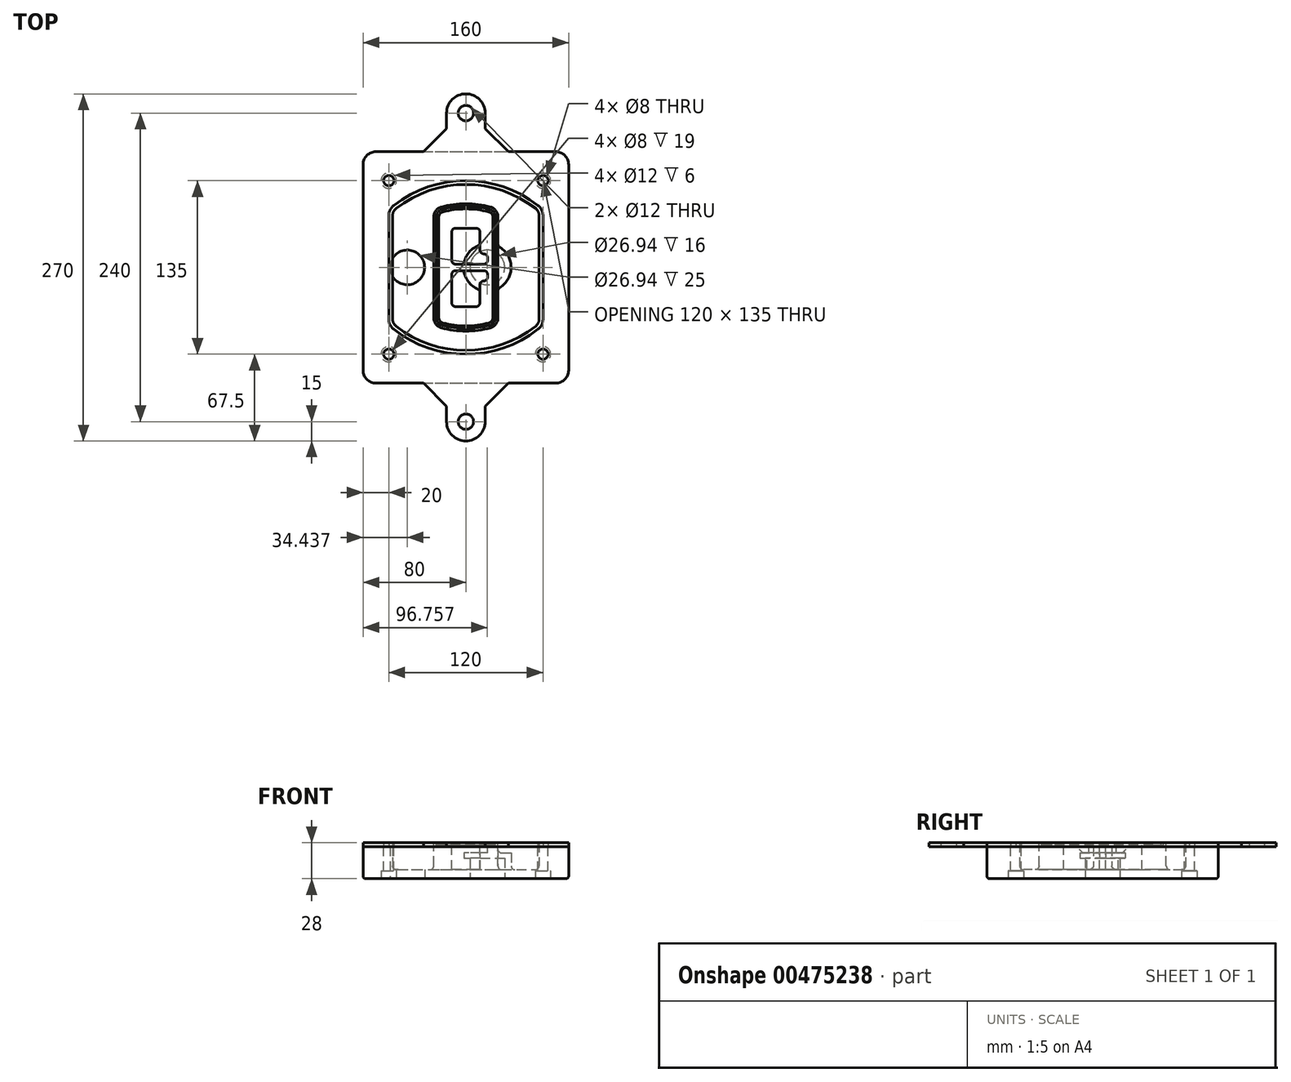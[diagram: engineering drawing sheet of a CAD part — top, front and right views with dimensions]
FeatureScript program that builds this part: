
annotation { "Feature Type Name" : "Feature", "Feature Type Description" : "" }
export const myFeature = defineFeature(function(context is Context, id is Id, definition is map)
    precondition{}
    {
        {
            var Q0;
            Q0=qCreatedBy(makeId("Top.planeOp"),FACE);
            var sketch = newSketch(context, id + "F0", { "sketchPlane" : qUnion([Q0])});
            skPoint(sketch, "E0.rect.middle", {"position": v(0, 0) * mm});
            skLineSegment(sketch, "E1.bottom", {"start": v(-70, -90) * mm, "end": v(70, -90) * mm});
            skLineSegment(sketch, "E1.top", {"start": v(-70, 90) * mm, "end": v(70, 90) * mm});
            skLineSegment(sketch, "E1.left", {"start": v(-80, -80) * mm, "end": v(-80, 80) * mm});
            skLineSegment(sketch, "E1.right", {"start": v(80, -80) * mm, "end": v(80, 80) * mm});
            skLineSegment(sketch, "E2", {"start": v(-80, 90) * mm, "end": v(80, -90) * mm, "construction": true});
            skLineSegment(sketch, "E3", {"start": v(80, 90) * mm, "end": v(-80, -90) * mm, "construction": true});
            skCircle(sketch, "E4", {"center": v(-60, 67.5) * mm, "radius": 4 * mm});
            skCircle(sketch, "E5", {"center": v(60, 67.5) * mm, "radius": 4 * mm});
            skCircle(sketch, "E6", {"center": v(60, -67.5) * mm, "radius": 4 * mm});
            skCircle(sketch, "E7", {"center": v(-60, -67.5) * mm, "radius": 4 * mm});
            skLineSegment(sketch, "E8", {"start": v(-60, 67.5) * mm, "end": v(60, 67.5) * mm, "construction": true});
            skLineSegment(sketch, "E9", {"start": v(60, 67.5) * mm, "end": v(60, -67.5) * mm, "construction": true});
            skLineSegment(sketch, "E10", {"start": v(60, -67.5) * mm, "end": v(-60, -67.5) * mm, "construction": true});
            skLineSegment(sketch, "E11", {"start": v(-60, -67.5) * mm, "end": v(-60, 67.5) * mm, "construction": true});
            skLineSegment(sketch, "E12", {"start": v(-60, 40.3) * mm, "end": v(-60, -40.3) * mm});
            skLineSegment(sketch, "E13", {"start": v(60, 40.3) * mm, "end": v(60, -40.3) * mm});
            skArc(sketch, "E14", {"start": v(56.15, 48.18) * mm, "mid": v(0, 67.5) * mm, "end": v(-56.15, 48.18) * mm});
            skArc(sketch, "E15", {"start": v(-56.15, -48.18) * mm, "mid": v(0, -67.5) * mm, "end": v(56.15, -48.18) * mm});
            skLineSegment(sketch, "E16", {"start": v(-60, 0) * mm, "end": v(60, 0) * mm, "construction": true});
            skPoint(sketch, "E17.visualSharp", {"position": v(-60, -45) * mm});
            skArc(sketch, "E17.filletArc", {"start": v(-60, -40.3) * mm, "mid": v(-58.99, -44.68) * mm, "end": v(-56.15, -48.18) * mm});
            skPoint(sketch, "E18.visualSharp", {"position": v(-60, 45) * mm});
            skArc(sketch, "E18.filletArc", {"start": v(-56.15, 48.18) * mm, "mid": v(-58.99, 44.68) * mm, "end": v(-60, 40.3) * mm});
            skPoint(sketch, "E19.visualSharp", {"position": v(60, 45) * mm});
            skArc(sketch, "E19.filletArc", {"start": v(60, 40.3) * mm, "mid": v(58.99, 44.68) * mm, "end": v(56.15, 48.18) * mm});
            skPoint(sketch, "E20.visualSharp", {"position": v(60, -45) * mm});
            skArc(sketch, "E20.filletArc", {"start": v(56.15, -48.18) * mm, "mid": v(58.99, -44.68) * mm, "end": v(60, -40.3) * mm});
            skPoint(sketch, "E21.visualSharp", {"position": v(-80, 90) * mm});
            skArc(sketch, "E21.filletArc", {"start": v(-70, 90) * mm, "mid": v(-77.07, 87.07) * mm, "end": v(-80, 80) * mm});
            skPoint(sketch, "E22.visualSharp", {"position": v(80, 90) * mm});
            skArc(sketch, "E22.filletArc", {"start": v(80, 80) * mm, "mid": v(77.07, 87.07) * mm, "end": v(70, 90) * mm});
            skPoint(sketch, "E23.visualSharp", {"position": v(80, -90) * mm});
            skArc(sketch, "E23.filletArc", {"start": v(70, -90) * mm, "mid": v(77.07, -87.07) * mm, "end": v(80, -80) * mm});
            skPoint(sketch, "E24.visualSharp", {"position": v(-80, -90) * mm});
            skArc(sketch, "E24.filletArc", {"start": v(-80, -80) * mm, "mid": v(-77.07, -87.07) * mm, "end": v(-70, -90) * mm});
            skArc(sketch, "E25.0", {"start": v(57, 40.3) * mm, "mid": v(56.3, 43.36) * mm, "end": v(54.3, 45.81) * mm});
            skLineSegment(sketch, "E25.1", {"start": v(57, 40.3) * mm, "end": v(57, -40.3) * mm});
            skArc(sketch, "E25.2", {"start": v(54.3, -45.81) * mm, "mid": v(56.3, -43.36) * mm, "end": v(57, -40.3) * mm});
            skArc(sketch, "E25.3", {"start": v(-54.3, -45.81) * mm, "mid": v(0, -64.5) * mm, "end": v(54.3, -45.81) * mm});
            skArc(sketch, "E25.4", {"start": v(-57, -40.3) * mm, "mid": v(-56.3, -43.36) * mm, "end": v(-54.3, -45.81) * mm});
            skArc(sketch, "E25.5", {"start": v(54.3, 45.81) * mm, "mid": v(0, 64.5) * mm, "end": v(-54.3, 45.81) * mm});
            skLineSegment(sketch, "E25.6", {"start": v(-57, 40.3) * mm, "end": v(-57, -40.3) * mm});
            skArc(sketch, "E25.7", {"start": v(-54.3, 45.81) * mm, "mid": v(-56.3, 43.36) * mm, "end": v(-57, 40.3) * mm});
            skArc(sketch, "E26.0", {"start": v(-58.62, 51.33) * mm, "mid": v(-62.58, 46.43) * mm, "end": v(-64, 40.3) * mm});
            skArc(sketch, "E26.1", {"start": v(58.62, 51.33) * mm, "mid": v(0, 71.5) * mm, "end": v(-58.62, 51.33) * mm});
            skArc(sketch, "E26.2", {"start": v(64, 40.3) * mm, "mid": v(62.58, 46.43) * mm, "end": v(58.62, 51.33) * mm});
            skLineSegment(sketch, "E26.3", {"start": v(64, 40.3) * mm, "end": v(64, -40.3) * mm});
            skArc(sketch, "E26.4", {"start": v(58.62, -51.33) * mm, "mid": v(62.58, -46.43) * mm, "end": v(64, -40.3) * mm});
            skLineSegment(sketch, "E26.5", {"start": v(-64, 40.3) * mm, "end": v(-64, -40.3) * mm});
            skArc(sketch, "E26.6", {"start": v(-58.62, -51.33) * mm, "mid": v(0, -71.5) * mm, "end": v(58.62, -51.33) * mm});
            skArc(sketch, "E26.7", {"start": v(-64, -40.3) * mm, "mid": v(-62.58, -46.43) * mm, "end": v(-58.62, -51.33) * mm});
            skSolve(sketch);
        }
        {
            var Q0;
            Q0=makeQuery(id+"F0.imprint","IMPRINT",FACE,{"disambiguationData":[TD([[makeQuery(id+"F0.imprint","IMPRINT",EDGE,{"derivedFrom":sQuery(id+"F0.wireOp",EDGE,"E1.bottom")}),1.0]])]});
            var Q1;
            Q1=makeQuery(id+"F0.imprint","IMPRINT",FACE,{"disambiguationData":[TD([[makeQuery(id+"F0.imprint","IMPRINT",EDGE,{"derivedFrom":sQuery(id+"F0.wireOp",EDGE,"E12")}),1.0]])]});
            var Q2;
            Q2=makeQuery(id+"F0.imprint","IMPRINT",FACE,{"disambiguationData":[TD([[makeQuery(id+"F0.imprint","IMPRINT",EDGE,{"derivedFrom":sQuery(id+"F0.wireOp",EDGE,"E25.0")}),1.0]])]});
            var Q3;
            Q3=makeQuery(id+"F0.imprint","IMPRINT",FACE,{"disambiguationData":[TD([[makeQuery(id+"F0.imprint","IMPRINT",EDGE,{"derivedFrom":sQuery(id+"F0.wireOp",EDGE,"E12")}),-1.0]])]});
            extrude(context, id + "F1", {"entities" : qUnion([Q0, Q1, Q2, Q3]), "oppositeDirection" : true, "depth" : 25 * mm});
        }
        {
            var Q0;
            Q0=makeQuery(id+"F0.imprint","IMPRINT",FACE,{"disambiguationData":[TD([[makeQuery(id+"F0.imprint","IMPRINT",EDGE,{"derivedFrom":sQuery(id+"F0.wireOp",EDGE,"E12")}),1.0]])]});
            extrude(context, id + "F2", {"entities" : qUnion([Q0]), "operationType" : NewBodyOperationType.ADD, "depth" : 3 * mm});
        }
        {
            var Q0;
            Q0=makeQuery(id+"F0.imprint","IMPRINT",FACE,{"disambiguationData":[TD([[makeQuery(id+"F0.imprint","IMPRINT",EDGE,{"derivedFrom":sQuery(id+"F0.wireOp",EDGE,"E25.0")}),1.0]])]});
            extrude(context, id + "F3", {"entities" : qUnion([Q0]), "operationType" : NewBodyOperationType.REMOVE, "oppositeDirection" : true, "depth" : 18 * mm});
        }
        {
            var Q0;
            Q0=makeQuery(id+"F2.opExtrude","CAP_FACE",FACE,{"disambiguationData":[OSD([sQuery(id+"F0.wireOp",EDGE,"E12"),sQuery(id+"F0.wireOp",EDGE,"E13"),sQuery(id+"F0.wireOp",EDGE,"E14"),sQuery(id+"F0.wireOp",EDGE,"E15"),sQuery(id+"F0.wireOp",EDGE,"E17.filletArc"),sQuery(id+"F0.wireOp",EDGE,"E18.filletArc"),sQuery(id+"F0.wireOp",EDGE,"E19.filletArc"),sQuery(id+"F0.wireOp",EDGE,"E20.filletArc"),sQuery(id+"F0.wireOp",EDGE,"E25.0"),sQuery(id+"F0.wireOp",EDGE,"E25.1"),sQuery(id+"F0.wireOp",EDGE,"E25.2"),sQuery(id+"F0.wireOp",EDGE,"E25.3"),sQuery(id+"F0.wireOp",EDGE,"E25.4"),sQuery(id+"F0.wireOp",EDGE,"E25.5"),sQuery(id+"F0.wireOp",EDGE,"E25.6"),sQuery(id+"F0.wireOp",EDGE,"E25.7")])],"isStart":false});
            var sketch = newSketch(context, id + "F4", { "sketchPlane" : qUnion([Q0])});
            skArc(sketch, "E27.0", {"start": v(-19.08, -46.97) * mm, "mid": v(0, -49.5) * mm, "end": v(19.08, -46.97) * mm});
            skArc(sketch, "E28.0", {"start": v(19.08, 46.97) * mm, "mid": v(0, 49.5) * mm, "end": v(-19.08, 46.97) * mm});
            skLineSegment(sketch, "E29", {"start": v(-25, 39.25) * mm, "end": v(-25, -39.25) * mm});
            skLineSegment(sketch, "E30", {"start": v(25, 39.25) * mm, "end": v(25, -39.25) * mm});
            skLineSegment(sketch, "E31", {"start": v(-25, 45.1) * mm, "end": v(25, 45.1) * mm, "construction": true});
            skLineSegment(sketch, "E32", {"start": v(-25, -45.1) * mm, "end": v(25, -45.1) * mm, "construction": true});
            skPoint(sketch, "E33.visualSharp", {"position": v(-25, 45.1) * mm});
            skArc(sketch, "E33.filletArc", {"start": v(-19.08, 46.97) * mm, "mid": v(-23.35, 44.11) * mm, "end": v(-25, 39.25) * mm});
            skPoint(sketch, "E34.visualSharp", {"position": v(25, 45.1) * mm});
            skArc(sketch, "E34.filletArc", {"start": v(25, 39.25) * mm, "mid": v(23.35, 44.11) * mm, "end": v(19.08, 46.97) * mm});
            skPoint(sketch, "E35.visualSharp", {"position": v(25, -45.1) * mm});
            skArc(sketch, "E35.filletArc", {"start": v(19.08, -46.97) * mm, "mid": v(23.35, -44.11) * mm, "end": v(25, -39.25) * mm});
            skPoint(sketch, "E36.visualSharp", {"position": v(-25, -45.1) * mm});
            skArc(sketch, "E36.filletArc", {"start": v(-25, -39.25) * mm, "mid": v(-23.35, -44.11) * mm, "end": v(-19.08, -46.97) * mm});
            skArc(sketch, "E37.0", {"start": v(54.3, 45.81) * mm, "mid": v(0, 64.5) * mm, "end": v(-54.3, 45.81) * mm});
            skArc(sketch, "E37.1", {"start": v(-54.3, 45.81) * mm, "mid": v(-56.3, 43.36) * mm, "end": v(-57, 40.3) * mm});
            skLineSegment(sketch, "E37.2", {"start": v(-57, 40.3) * mm, "end": v(-57, -40.3) * mm});
            skArc(sketch, "E37.3", {"start": v(-57, -40.3) * mm, "mid": v(-56.3, -43.36) * mm, "end": v(-54.3, -45.81) * mm});
            skArc(sketch, "E37.4", {"start": v(-54.3, -45.81) * mm, "mid": v(0, -64.5) * mm, "end": v(54.3, -45.81) * mm});
            skArc(sketch, "E37.5", {"start": v(54.3, -45.81) * mm, "mid": v(56.3, -43.36) * mm, "end": v(57, -40.3) * mm});
            skLineSegment(sketch, "E37.6", {"start": v(57, 40.3) * mm, "end": v(57, -40.3) * mm});
            skArc(sketch, "E37.7", {"start": v(57, 40.3) * mm, "mid": v(56.3, 43.36) * mm, "end": v(54.3, 45.81) * mm});
            skLineSegment(sketch, "E38.0", {"start": v(23, 39.25) * mm, "end": v(23, -39.25) * mm});
            skArc(sketch, "E38.1", {"start": v(18.56, -45.04) * mm, "mid": v(21.76, -42.9) * mm, "end": v(23, -39.25) * mm});
            skArc(sketch, "E38.2", {"start": v(-18.56, -45.04) * mm, "mid": v(0, -47.5) * mm, "end": v(18.56, -45.04) * mm});
            skArc(sketch, "E38.3", {"start": v(-23, -39.25) * mm, "mid": v(-21.76, -42.9) * mm, "end": v(-18.56, -45.04) * mm});
            skLineSegment(sketch, "E38.4", {"start": v(-23, 39.25) * mm, "end": v(-23, -39.25) * mm});
            skArc(sketch, "E38.5", {"start": v(23, 39.25) * mm, "mid": v(21.76, 42.9) * mm, "end": v(18.56, 45.04) * mm});
            skArc(sketch, "E38.6", {"start": v(-18.56, 45.04) * mm, "mid": v(-21.76, 42.9) * mm, "end": v(-23, 39.25) * mm});
            skArc(sketch, "E38.7", {"start": v(18.56, 45.04) * mm, "mid": v(0, 47.5) * mm, "end": v(-18.56, 45.04) * mm});
            skArc(sketch, "E39.0", {"start": v(21, 39.25) * mm, "mid": v(20.18, 41.68) * mm, "end": v(18.04, 43.1) * mm});
            skLineSegment(sketch, "E39.1", {"start": v(21, 39.25) * mm, "end": v(21, -39.25) * mm});
            skArc(sketch, "E39.2", {"start": v(18.04, -43.1) * mm, "mid": v(20.18, -41.68) * mm, "end": v(21, -39.25) * mm});
            skArc(sketch, "E39.3", {"start": v(-18.04, -43.1) * mm, "mid": v(0, -45.5) * mm, "end": v(18.04, -43.1) * mm});
            skArc(sketch, "E39.4", {"start": v(-21, -39.25) * mm, "mid": v(-20.18, -41.68) * mm, "end": v(-18.04, -43.1) * mm});
            skArc(sketch, "E39.5", {"start": v(18.04, 43.1) * mm, "mid": v(0, 45.5) * mm, "end": v(-18.04, 43.1) * mm});
            skLineSegment(sketch, "E39.6", {"start": v(-21, 39.25) * mm, "end": v(-21, -39.25) * mm});
            skArc(sketch, "E39.7", {"start": v(-18.04, 43.1) * mm, "mid": v(-20.18, 41.68) * mm, "end": v(-21, 39.25) * mm});
            skLineSegment(sketch, "E40", {"start": v(-25, 0) * mm, "end": v(25, 0) * mm, "construction": true});
            skLineSegment(sketch, "E41", {"start": v(-11, 5.5) * mm, "end": v(-11, 27.5) * mm});
            skLineSegment(sketch, "E42", {"start": v(-8, 30.5) * mm, "end": v(8, 30.5) * mm});
            skLineSegment(sketch, "E43", {"start": v(11, 27.5) * mm, "end": v(11, 13.5) * mm});
            skLineSegment(sketch, "E44", {"start": v(14, 10.5) * mm, "end": v(14, 10.5) * mm});
            skLineSegment(sketch, "E45", {"start": v(17, 7.5) * mm, "end": v(17, 5.5) * mm});
            skLineSegment(sketch, "E46", {"start": v(14, 2.5) * mm, "end": v(-8, 2.5) * mm});
            skPoint(sketch, "E47.visualSharp", {"position": v(-11, 30.5) * mm});
            skArc(sketch, "E47.filletArc", {"start": v(-8, 30.5) * mm, "mid": v(-10.12, 29.62) * mm, "end": v(-11, 27.5) * mm});
            skPoint(sketch, "E48.visualSharp", {"position": v(11, 30.5) * mm});
            skArc(sketch, "E48.filletArc", {"start": v(11, 27.5) * mm, "mid": v(10.12, 29.62) * mm, "end": v(8, 30.5) * mm});
            skPoint(sketch, "E49.visualSharp", {"position": v(11, 10.5) * mm});
            skArc(sketch, "E49.filletArc", {"start": v(11, 13.5) * mm, "mid": v(11.88, 11.38) * mm, "end": v(14, 10.5) * mm});
            skPoint(sketch, "E50.visualSharp", {"position": v(17, 10.5) * mm});
            skArc(sketch, "E50.filletArc", {"start": v(17, 7.5) * mm, "mid": v(16.12, 9.62) * mm, "end": v(14, 10.5) * mm});
            skPoint(sketch, "E51.visualSharp", {"position": v(17, 2.5) * mm});
            skArc(sketch, "E51.filletArc", {"start": v(14, 2.5) * mm, "mid": v(16.12, 3.38) * mm, "end": v(17, 5.5) * mm});
            skPoint(sketch, "E52.visualSharp", {"position": v(-11, 2.5) * mm});
            skArc(sketch, "E52.filletArc", {"start": v(-11, 5.5) * mm, "mid": v(-10.12, 3.38) * mm, "end": v(-8, 2.5) * mm});
            skLineSegment(sketch, "E53.0.MirrorCS", {"start": v(14, -2.5) * mm, "end": v(-8, -2.5) * mm});
            skArc(sketch, "E54.0.MirrorCS", {"start": v(-11, -5.5) * mm, "mid": v(-10.12, -3.38) * mm, "end": v(-8, -2.5) * mm});
            skLineSegment(sketch, "E55.0.MirrorCS", {"start": v(-11, -5.5) * mm, "end": v(-11, -27.5) * mm});
            skArc(sketch, "E56.0.MirrorCS", {"start": v(-8, -30.5) * mm, "mid": v(-10.12, -29.62) * mm, "end": v(-11, -27.5) * mm});
            skLineSegment(sketch, "E57.0.MirrorCS", {"start": v(-8, -30.5) * mm, "end": v(8, -30.5) * mm});
            skArc(sketch, "E58.0.MirrorCS", {"start": v(11, -27.5) * mm, "mid": v(10.12, -29.62) * mm, "end": v(8, -30.5) * mm});
            skLineSegment(sketch, "E59.0.MirrorCS", {"start": v(11, -27.5) * mm, "end": v(11, -13.5) * mm});
            skArc(sketch, "E60.0.MirrorCS", {"start": v(11, -13.5) * mm, "mid": v(11.88, -11.38) * mm, "end": v(14, -10.5) * mm});
            skArc(sketch, "E61.0.MirrorCS", {"start": v(17, -7.5) * mm, "mid": v(16.12, -9.62) * mm, "end": v(14, -10.5) * mm});
            skLineSegment(sketch, "E62.0.MirrorCS", {"start": v(17, -7.5) * mm, "end": v(17, -5.5) * mm});
            skArc(sketch, "E63.0.MirrorCS", {"start": v(14, -2.5) * mm, "mid": v(16.12, -3.38) * mm, "end": v(17, -5.5) * mm});
            skSolve(sketch);
        }
        {
            var Q0;
            Q0=makeQuery(id+"F4.imprint","IMPRINT",FACE,{"disambiguationData":[TD([[makeQuery(id+"F4.imprint","IMPRINT",EDGE,{"derivedFrom":sQuery(id+"F4.wireOp",EDGE,"E27.0")}),1.0]])]});
            var Q1;
            Q1=makeQuery(id+"F4.imprint","IMPRINT",FACE,{"disambiguationData":[TD([[makeQuery(id+"F4.imprint","IMPRINT",EDGE,{"derivedFrom":sQuery(id+"F4.wireOp",EDGE,"E38.0")}),-1.0]])]});
            var Q2;
            Q2=makeQuery(id+"F4.imprint","IMPRINT",FACE,{"disambiguationData":[TD([[makeQuery(id+"F4.imprint","IMPRINT",EDGE,{"derivedFrom":sQuery(id+"F4.wireOp",EDGE,"E39.0")}),1.0]])]});
            extrude(context, id + "F5", {"entities" : qUnion([Q0, Q1, Q2]), "operationType" : NewBodyOperationType.ADD, "endBound" : BoundingType.UP_TO_NEXT, "oppositeDirection" : true, "depth" : 25 * mm});
        }
        {
            var Q0;
            Q0=makeQuery(id+"F4.imprint","IMPRINT",FACE,{"disambiguationData":[TD([[makeQuery(id+"F4.imprint","IMPRINT",EDGE,{"derivedFrom":sQuery(id+"F4.wireOp",EDGE,"E38.0")}),-1.0]])]});
            extrude(context, id + "F6", {"entities" : qUnion([Q0]), "operationType" : NewBodyOperationType.REMOVE, "oppositeDirection" : true, "depth" : 2 * mm});
        }
        {
            var Q0;
            Q0=makeQuery(id+"F1.opExtrude","CAP_FACE",FACE,{"disambiguationData":[OSD([sQuery(id+"F0.wireOp",EDGE,"E1.bottom"),sQuery(id+"F0.wireOp",EDGE,"E1.top"),sQuery(id+"F0.wireOp",EDGE,"E1.left"),sQuery(id+"F0.wireOp",EDGE,"E1.right"),sQuery(id+"F0.wireOp",EDGE,"E4"),sQuery(id+"F0.wireOp",EDGE,"E5"),sQuery(id+"F0.wireOp",EDGE,"E6"),sQuery(id+"F0.wireOp",EDGE,"E7"),sQuery(id+"F0.wireOp",EDGE,"E21.filletArc"),sQuery(id+"F0.wireOp",EDGE,"E22.filletArc"),sQuery(id+"F0.wireOp",EDGE,"E23.filletArc"),sQuery(id+"F0.wireOp",EDGE,"E24.filletArc")])],"isStart":false});
            var sketch = newSketch(context, id + "F7", { "sketchPlane" : qUnion([Q0])});
            skCircle(sketch, "E64", {"center": v(16.76, 0) * mm, "radius": 13.47 * mm});
            skCircle(sketch, "E65", {"center": v(-45.56, 0) * mm, "radius": 13.47 * mm});
            skLineSegment(sketch, "E66", {"start": v(80, 0) * mm, "end": v(-80, 0) * mm});
            skCircle(sketch, "E67", {"center": v(16.76, 0) * mm, "radius": 18.47 * mm});
            skCircle(sketch, "E68", {"center": v(60, -67.5) * mm, "radius": 6 * mm});
            skCircle(sketch, "E69", {"center": v(-60, -67.5) * mm, "radius": 6 * mm});
            skCircle(sketch, "E70", {"center": v(-60, 67.5) * mm, "radius": 6 * mm});
            skCircle(sketch, "E71", {"center": v(60, 67.5) * mm, "radius": 6 * mm});
            skSolve(sketch);
        }
        {
            var Q0;
            {var subQ1=sQuery(id+"F7.wireOp",EDGE,"E66");var subQ4=sQuery(id+"F7.wireOp",EDGE,"E64");var subQ6=makeQuery(id+"F7.imprint","INTERSECT",VERTEX,{"disambiguationData":[OD(0.0)],"derivedFrom":[subQ4,subQ1]});Q0=makeQuery(id+"F7.imprint","IMPRINT",FACE,{"disambiguationData":[TD([[makeQuery(id+"F7.imprint","IMPRINT",EDGE,{"disambiguationData":[TD([[subQ6,-1.0]])],"derivedFrom":subQ4}),-1.0]])]});}
            var Q1;
            {var subQ0=sQuery(id+"F7.wireOp",EDGE,"E66");var subQ1=sQuery(id+"F7.wireOp",EDGE,"E64");var subQ3=makeQuery(id+"F7.imprint","INTERSECT",VERTEX,{"disambiguationData":[OD(0.0)],"derivedFrom":[subQ1,subQ0]});Q1=makeQuery(id+"F7.imprint","IMPRINT",FACE,{"disambiguationData":[TD([[makeQuery(id+"F7.imprint","IMPRINT",EDGE,{"disambiguationData":[TD([[subQ3,-1.0]])],"derivedFrom":subQ1}),1.0]])]});}
            var Q2;
            {var subQ0=sQuery(id+"F7.wireOp",EDGE,"E66");var subQ1=sQuery(id+"F7.wireOp",EDGE,"E64");var subQ3=makeQuery(id+"F7.imprint","INTERSECT",VERTEX,{"disambiguationData":[OD(0.0)],"derivedFrom":[subQ1,subQ0]});Q2=makeQuery(id+"F7.imprint","IMPRINT",FACE,{"disambiguationData":[TD([[makeQuery(id+"F7.imprint","IMPRINT",EDGE,{"disambiguationData":[TD([[subQ3,1.0]])],"derivedFrom":subQ1}),1.0]])]});}
            var Q3;
            {var subQ1=sQuery(id+"F7.wireOp",EDGE,"E66");var subQ4=sQuery(id+"F7.wireOp",EDGE,"E64");var subQ6=makeQuery(id+"F7.imprint","INTERSECT",VERTEX,{"disambiguationData":[OD(0.0)],"derivedFrom":[subQ4,subQ1]});Q3=makeQuery(id+"F7.imprint","IMPRINT",FACE,{"disambiguationData":[TD([[makeQuery(id+"F7.imprint","IMPRINT",EDGE,{"disambiguationData":[TD([[subQ6,1.0]])],"derivedFrom":subQ4}),-1.0]])]});}
            extrude(context, id + "F8", {"entities" : qUnion([Q0, Q1, Q2, Q3]), "operationType" : NewBodyOperationType.ADD, "oppositeDirection" : true, "depth" : 20 * mm});
        }
        {
            var Q0;
            {var subQ0=sQuery(id+"F7.wireOp",EDGE,"E66");var subQ1=sQuery(id+"F7.wireOp",EDGE,"E64");var subQ3=makeQuery(id+"F7.imprint","INTERSECT",VERTEX,{"disambiguationData":[OD(0.0)],"derivedFrom":[subQ1,subQ0]});Q0=makeQuery(id+"F7.imprint","IMPRINT",FACE,{"disambiguationData":[TD([[makeQuery(id+"F7.imprint","IMPRINT",EDGE,{"disambiguationData":[TD([[subQ3,-1.0]])],"derivedFrom":subQ1}),1.0]])]});}
            var Q1;
            {var subQ0=sQuery(id+"F7.wireOp",EDGE,"E66");var subQ1=sQuery(id+"F7.wireOp",EDGE,"E64");var subQ3=makeQuery(id+"F7.imprint","INTERSECT",VERTEX,{"disambiguationData":[OD(0.0)],"derivedFrom":[subQ1,subQ0]});Q1=makeQuery(id+"F7.imprint","IMPRINT",FACE,{"disambiguationData":[TD([[makeQuery(id+"F7.imprint","IMPRINT",EDGE,{"disambiguationData":[TD([[subQ3,1.0]])],"derivedFrom":subQ1}),1.0]])]});}
            extrude(context, id + "F9", {"entities" : qUnion([Q0, Q1]), "operationType" : NewBodyOperationType.REMOVE, "oppositeDirection" : true, "depth" : 16 * mm});
        }
        {
            var Q0;
            {var subQ0=sQuery(id+"F7.wireOp",EDGE,"E66");var subQ1=sQuery(id+"F7.wireOp",EDGE,"E65");var subQ3=makeQuery(id+"F7.imprint","INTERSECT",VERTEX,{"disambiguationData":[OD(0.0)],"derivedFrom":[subQ1,subQ0]});Q0=makeQuery(id+"F7.imprint","IMPRINT",FACE,{"disambiguationData":[TD([[makeQuery(id+"F7.imprint","IMPRINT",EDGE,{"disambiguationData":[TD([[subQ3,-1.0]])],"derivedFrom":subQ1}),1.0]])]});}
            var Q1;
            {var subQ0=sQuery(id+"F7.wireOp",EDGE,"E66");var subQ1=sQuery(id+"F7.wireOp",EDGE,"E65");var subQ3=makeQuery(id+"F7.imprint","INTERSECT",VERTEX,{"disambiguationData":[OD(0.0)],"derivedFrom":[subQ1,subQ0]});Q1=makeQuery(id+"F7.imprint","IMPRINT",FACE,{"disambiguationData":[TD([[makeQuery(id+"F7.imprint","IMPRINT",EDGE,{"disambiguationData":[TD([[subQ3,1.0]])],"derivedFrom":subQ1}),1.0]])]});}
            extrude(context, id + "F10", {"entities" : qUnion([Q0, Q1]), "operationType" : NewBodyOperationType.REMOVE, "oppositeDirection" : true, "depth" : 25 * mm});
        }
        {
            var Q0;
            Q0=makeQuery(id+"F7.imprint","IMPRINT",FACE,{"disambiguationData":[TD([[makeQuery(id+"F7.imprint","IMPRINT",EDGE,{"derivedFrom":sQuery(id+"F7.wireOp",EDGE,"E68")}),1.0]])]});
            var Q1;
            Q1=makeQuery(id+"F7.imprint","IMPRINT",FACE,{"disambiguationData":[TD([[makeQuery(id+"F7.imprint","IMPRINT",EDGE,{"derivedFrom":makeQuery(id+"F1.opExtrude","CAP_EDGE",EDGE,{"disambiguationData":[OSD([sQuery(id+"F0.wireOp",EDGE,"E5")])],"isStart":false})}),-1.0]])]});
            var Q2;
            Q2=makeQuery(id+"F7.imprint","IMPRINT",FACE,{"disambiguationData":[TD([[makeQuery(id+"F7.imprint","IMPRINT",EDGE,{"derivedFrom":sQuery(id+"F7.wireOp",EDGE,"E69")}),1.0]])]});
            var Q3;
            Q3=makeQuery(id+"F7.imprint","IMPRINT",FACE,{"disambiguationData":[TD([[makeQuery(id+"F7.imprint","IMPRINT",EDGE,{"derivedFrom":makeQuery(id+"F1.opExtrude","CAP_EDGE",EDGE,{"disambiguationData":[OSD([sQuery(id+"F0.wireOp",EDGE,"E4")])],"isStart":false})}),-1.0]])]});
            var Q4;
            Q4=makeQuery(id+"F7.imprint","IMPRINT",FACE,{"disambiguationData":[TD([[makeQuery(id+"F7.imprint","IMPRINT",EDGE,{"derivedFrom":sQuery(id+"F7.wireOp",EDGE,"E70")}),1.0]])]});
            var Q5;
            Q5=makeQuery(id+"F7.imprint","IMPRINT",FACE,{"disambiguationData":[TD([[makeQuery(id+"F7.imprint","IMPRINT",EDGE,{"derivedFrom":makeQuery(id+"F1.opExtrude","CAP_EDGE",EDGE,{"disambiguationData":[OSD([sQuery(id+"F0.wireOp",EDGE,"E7")])],"isStart":false})}),-1.0]])]});
            var Q6;
            Q6=makeQuery(id+"F7.imprint","IMPRINT",FACE,{"disambiguationData":[TD([[makeQuery(id+"F7.imprint","IMPRINT",EDGE,{"derivedFrom":sQuery(id+"F7.wireOp",EDGE,"E71")}),1.0]])]});
            var Q7;
            Q7=makeQuery(id+"F7.imprint","IMPRINT",FACE,{"disambiguationData":[TD([[makeQuery(id+"F7.imprint","IMPRINT",EDGE,{"derivedFrom":makeQuery(id+"F1.opExtrude","CAP_EDGE",EDGE,{"disambiguationData":[OSD([sQuery(id+"F0.wireOp",EDGE,"E6")])],"isStart":false})}),-1.0]])]});
            extrude(context, id + "F11", {"entities" : qUnion([Q0, Q1, Q2, Q3, Q4, Q5, Q6, Q7]), "operationType" : NewBodyOperationType.REMOVE, "oppositeDirection" : true, "depth" : 6 * mm});
        }
        {
            var Q0;
            Q0=makeQuery(id+"F9.boolean.opBoolean","COPY",FACE,{"derivedFrom":makeQuery(id+"F9.opExtrude","CAP_FACE",FACE,{"disambiguationData":[OSD([sQuery(id+"F7.wireOp",EDGE,"E64")])],"isStart":false})});
            var sketch = newSketch(context, id + "F12", { "sketchPlane" : qUnion([Q0])});
            skArc(sketch, "E72.0", {"start": v(11, 17.55) * mm, "mid": v(2.57, 11.82) * mm, "end": v(-1.54, 2.5) * mm});
            skArc(sketch, "E72.1", {"start": v(-1.54, -2.5) * mm, "mid": v(2.57, -11.82) * mm, "end": v(11, -17.55) * mm});
            skLineSegment(sketch, "E73", {"start": v(-1.54, -2.5) * mm, "end": v(14, -2.5) * mm});
            skLineSegment(sketch, "E74.0", {"start": v(14, 2.5) * mm, "end": v(-1.54, 2.5) * mm});
            skArc(sketch, "E74.1", {"start": v(14, 2.5) * mm, "mid": v(16.12, 3.38) * mm, "end": v(17, 5.5) * mm});
            skLineSegment(sketch, "E74.2", {"start": v(17, 7.5) * mm, "end": v(17, 5.5) * mm});
            skArc(sketch, "E74.3", {"start": v(17, 7.5) * mm, "mid": v(16.12, 9.62) * mm, "end": v(14, 10.5) * mm});
            skArc(sketch, "E74.4", {"start": v(11, 13.5) * mm, "mid": v(11.88, 11.38) * mm, "end": v(14, 10.5) * mm});
            skLineSegment(sketch, "E74.5", {"start": v(11, 17.55) * mm, "end": v(11, 13.5) * mm});
            skLineSegment(sketch, "E74.7", {"start": v(14, -2.5) * mm, "end": v(-1.54, -2.5) * mm});
            skArc(sketch, "E74.8", {"start": v(14, -2.5) * mm, "mid": v(16.12, -3.38) * mm, "end": v(17, -5.5) * mm});
            skLineSegment(sketch, "E74.9", {"start": v(17, -7.5) * mm, "end": v(17, -5.5) * mm});
            skArc(sketch, "E74.10", {"start": v(17, -7.5) * mm, "mid": v(16.12, -9.62) * mm, "end": v(14, -10.5) * mm});
            skArc(sketch, "E74.11", {"start": v(11, -13.5) * mm, "mid": v(11.88, -11.38) * mm, "end": v(14, -10.5) * mm});
            skLineSegment(sketch, "E74.12", {"start": v(11, -17.55) * mm, "end": v(11, -13.5) * mm});
            skPoint(sketch, "E75.orphan", {"position": v(11, -27.5) * mm});
            skPoint(sketch, "E76.orphan", {"position": v(-8, -2.5) * mm});
            skPoint(sketch, "E77.orphan", {"position": v(-8, 2.5) * mm});
            skPoint(sketch, "E78.orphan", {"position": v(11, 27.5) * mm});
            skSolve(sketch);
        }
        {
            var Q0;
            {var subQ7=sQuery(id+"F12.wireOp",EDGE,"E72.0");var subQ14=sQuery(id+"F12.wireOp",EDGE,"E72.1");var subQ16=sQuery(id+"F12.wireOp",EDGE,"E74.1");var subQ18=sQuery(id+"F12.wireOp",EDGE,"E74.8");Q0=qUnion([makeQuery(id+"F12.imprint","IMPRINT",FACE,{"disambiguationData":[TD([[makeQuery(id+"F12.imprint","IMPRINT",EDGE,{"derivedFrom":subQ7}),1.0]])]}),makeQuery(id+"F12.imprint","IMPRINT",FACE,{"disambiguationData":[TD([[makeQuery(id+"F12.imprint","IMPRINT",EDGE,{"derivedFrom":subQ14}),1.0]])]}),makeQuery(id+"F12.imprint","IMPRINT",FACE,{"disambiguationData":[TD([[makeQuery(id+"F12.imprint","IMPRINT",EDGE,{"derivedFrom":subQ16}),1.0]])]}),makeQuery(id+"F12.imprint","IMPRINT",FACE,{"disambiguationData":[TD([[makeQuery(id+"F12.imprint","IMPRINT",EDGE,{"derivedFrom":subQ18}),-1.0]])]})]);}
            var Q1;
            Q1=makeQuery(id+"F5.boolean.opBoolean","SPLIT",FACE,{"disambiguationData":[TD([makeQuery(id+"F5.opExtrude","SWEPT_FACE",FACE,{"disambiguationData":[OSD([sQuery(id+"F4.wireOp",EDGE,"E41")])]})])],"derivedFrom":makeQuery(id+"F3.boolean.opBoolean","COPY",FACE,{"derivedFrom":makeQuery(id+"F3.opExtrude","CAP_FACE",FACE,{"disambiguationData":[OSD([sQuery(id+"F0.wireOp",EDGE,"E25.0"),sQuery(id+"F0.wireOp",EDGE,"E25.1"),sQuery(id+"F0.wireOp",EDGE,"E25.2"),sQuery(id+"F0.wireOp",EDGE,"E25.3"),sQuery(id+"F0.wireOp",EDGE,"E25.4"),sQuery(id+"F0.wireOp",EDGE,"E25.5"),sQuery(id+"F0.wireOp",EDGE,"E25.6"),sQuery(id+"F0.wireOp",EDGE,"E25.7")])],"isStart":false})})});
            extrude(context, id + "F13", {"entities" : qUnion([Q0]), "operationType" : NewBodyOperationType.REMOVE, "endBound" : BoundingType.UP_TO_SURFACE, "endBoundEntityFace" : qUnion([Q1]), "depth" : 25 * mm});
        }
        {
            var Q0;
            Q0=makeQuery(id+"F3.boolean.opBoolean","COPY",EDGE,{"derivedFrom":makeQuery(id+"F3.opExtrude","CAP_EDGE",EDGE,{"disambiguationData":[OSD([sQuery(id+"F0.wireOp",EDGE,"E25.6")])],"isStart":false})});
            var Q1;
            Q1=makeQuery(id+"F8.boolean.opBoolean","INTERSECT",EDGE,{"derivedFrom":[makeQuery(id+"F5.opExtrude","SWEPT_FACE",FACE,{"disambiguationData":[OSD([sQuery(id+"F4.wireOp",EDGE,"E30")])]}),makeQuery(id+"F8.opExtrude","CAP_FACE",FACE,{"disambiguationData":[OSD([sQuery(id+"F7.wireOp",EDGE,"E67")])],"isStart":false})]});
            var Q2;
            Q2=makeQuery(id+"F8.boolean.opBoolean","INTERSECT",EDGE,{"disambiguationData":[OD(1.0)],"derivedFrom":[makeQuery(id+"F5.opExtrude","SWEPT_FACE",FACE,{"disambiguationData":[OSD([sQuery(id+"F4.wireOp",EDGE,"E30")])]}),makeQuery(id+"F8.opExtrude","SWEPT_FACE",FACE,{"disambiguationData":[OSD([sQuery(id+"F7.wireOp",EDGE,"E67")])]})]});
            var Q3;
            {var subQ0=sQuery(id+"F4.wireOp",EDGE,"E30");Q3=makeQuery(id+"F8.boolean.opBoolean","SPLIT",EDGE,{"disambiguationData":[TD([makeQuery(id+"F5.opExtrude","SWEPT_FACE",FACE,{"disambiguationData":[OSD([sQuery(id+"F4.wireOp",EDGE,"E35.filletArc")])]})])],"derivedFrom":makeQuery(id+"F5.opExtrude","CAP_EDGE",EDGE,{"disambiguationData":[OSD([subQ0])],"isStart":false})});}
            var Q4;
            {var subQ0=sQuery(id+"F0.wireOp",EDGE,"E25.7");var subQ1=sQuery(id+"F0.wireOp",EDGE,"E25.1");var subQ2=sQuery(id+"F0.wireOp",EDGE,"E25.6");var subQ3=sQuery(id+"F0.wireOp",EDGE,"E25.5");var subQ4=sQuery(id+"F0.wireOp",EDGE,"E25.4");var subQ5=sQuery(id+"F0.wireOp",EDGE,"E25.0");var subQ6=sQuery(id+"F0.wireOp",EDGE,"E25.2");var subQ7=sQuery(id+"F0.wireOp",EDGE,"E25.3");Q4=makeQuery(id+"F8.boolean.opBoolean","INTERSECT",EDGE,{"derivedFrom":[makeQuery(id+"F5.boolean.opBoolean","SPLIT",FACE,{"disambiguationData":[TD([makeQuery(id+"F2.opExtrude","SWEPT_FACE",FACE,{"disambiguationData":[OSD([subQ5])]})])],"derivedFrom":makeQuery(id+"F3.boolean.opBoolean","COPY",FACE,{"derivedFrom":makeQuery(id+"F3.opExtrude","CAP_FACE",FACE,{"disambiguationData":[OSD([subQ5,subQ1,subQ6,subQ7,subQ4,subQ3,subQ2,subQ0])],"isStart":false})})}),makeQuery(id+"F8.opExtrude","SWEPT_FACE",FACE,{"disambiguationData":[OSD([sQuery(id+"F7.wireOp",EDGE,"E67")])]})]});}
            var Q5;
            Q5=makeQuery(id+"F8.boolean.opBoolean","INTERSECT",EDGE,{"disambiguationData":[OD(0.0)],"derivedFrom":[makeQuery(id+"F5.opExtrude","SWEPT_FACE",FACE,{"disambiguationData":[OSD([sQuery(id+"F4.wireOp",EDGE,"E30")])]}),makeQuery(id+"F8.opExtrude","SWEPT_FACE",FACE,{"disambiguationData":[OSD([sQuery(id+"F7.wireOp",EDGE,"E67")])]})]});
            fillet(context, id + "F14", {"entities" : qUnion([Q0, Q1, Q2, Q3, Q4, Q5]), "radius" : 3 * mm, "tangentPropagation" : true, "allowEdgeOverflow" : false});
        }
        {
            var Q0;
            Q0=makeQuery(id+"F1.opExtrude","CAP_EDGE",EDGE,{"disambiguationData":[OSD([sQuery(id+"F0.wireOp",EDGE,"E1.bottom")])],"isStart":false});
            fillet(context, id + "F15", {"entities" : qUnion([Q0]), "radius" : 2 * mm, "tangentPropagation" : true, "allowEdgeOverflow" : false});
        }
        {
            var Q0;
            {var subQ0=sQuery(id+"F0.wireOp",EDGE,"E21.filletArc");var subQ1=sQuery(id+"F0.wireOp",EDGE,"E7");var subQ2=sQuery(id+"F0.wireOp",EDGE,"E6");var subQ3=sQuery(id+"F0.wireOp",EDGE,"E5");var subQ4=sQuery(id+"F0.wireOp",EDGE,"E4");var subQ5=sQuery(id+"F0.wireOp",EDGE,"E22.filletArc");var subQ6=sQuery(id+"F0.wireOp",EDGE,"E1.bottom");var subQ7=sQuery(id+"F0.wireOp",EDGE,"E1.right");var subQ8=sQuery(id+"F0.wireOp",EDGE,"E1.top");var subQ9=sQuery(id+"F0.wireOp",EDGE,"E1.left");var subQ10=sQuery(id+"F0.wireOp",EDGE,"E23.filletArc");var subQ11=sQuery(id+"F0.wireOp",EDGE,"E24.filletArc");Q0=makeQuery(id+"F2.boolean.opBoolean","SPLIT",FACE,{"disambiguationData":[TD([makeQuery(id+"F1.opExtrude","SWEPT_FACE",FACE,{"disambiguationData":[OSD([subQ6])]})])],"derivedFrom":makeQuery(id+"F1.opExtrude","CAP_FACE",FACE,{"disambiguationData":[OSD([subQ6,subQ8,subQ9,subQ7,subQ4,subQ3,subQ2,subQ1,subQ0,subQ5,subQ10,subQ11])],"isStart":true})});}
            var sketch = newSketch(context, id + "F16", { "sketchPlane" : qUnion([Q0])});
            skLineSegment(sketch, "E79.0", {"start": v(-70, 90) * mm, "end": v(70, 90) * mm});
            skArc(sketch, "E79.1", {"start": v(-70, 90) * mm, "mid": v(-77.07, 87.07) * mm, "end": v(-80, 80) * mm});
            skLineSegment(sketch, "E79.2", {"start": v(80, -80) * mm, "end": v(80, 80) * mm});
            skArc(sketch, "E79.3", {"start": v(80, 80) * mm, "mid": v(77.07, 87.07) * mm, "end": v(70, 90) * mm});
            skLineSegment(sketch, "E79.4", {"start": v(-80, -80) * mm, "end": v(-80, 80) * mm});
            skArc(sketch, "E79.5", {"start": v(-80, -80) * mm, "mid": v(-77.07, -87.07) * mm, "end": v(-70, -90) * mm});
            skLineSegment(sketch, "E79.6", {"start": v(-70, -90) * mm, "end": v(70, -90) * mm});
            skArc(sketch, "E79.7", {"start": v(-56.15, -48.18) * mm, "mid": v(0, -67.5) * mm, "end": v(56.15, -48.18) * mm});
            skCircle(sketch, "E79.8", {"center": v(-60, -67.5) * mm, "radius": 4 * mm});
            skCircle(sketch, "E79.9", {"center": v(-60, 67.5) * mm, "radius": 4 * mm});
            skCircle(sketch, "E79.10", {"center": v(60, 67.5) * mm, "radius": 4 * mm});
            skCircle(sketch, "E79.11", {"center": v(60, -67.5) * mm, "radius": 4 * mm});
            skArc(sketch, "E79.12", {"start": v(70, -90) * mm, "mid": v(77.07, -87.07) * mm, "end": v(80, -80) * mm});
            skArc(sketch, "E79.13", {"start": v(56.15, -48.18) * mm, "mid": v(58.99, -44.68) * mm, "end": v(60, -40.3) * mm});
            skLineSegment(sketch, "E79.14", {"start": v(60, 40.3) * mm, "end": v(60, -40.3) * mm});
            skArc(sketch, "E79.15", {"start": v(60, 40.3) * mm, "mid": v(58.99, 44.68) * mm, "end": v(56.15, 48.18) * mm});
            skArc(sketch, "E79.16", {"start": v(56.15, 48.18) * mm, "mid": v(0, 67.5) * mm, "end": v(-56.15, 48.18) * mm});
            skArc(sketch, "E79.17", {"start": v(-56.15, 48.18) * mm, "mid": v(-58.99, 44.68) * mm, "end": v(-60, 40.3) * mm});
            skLineSegment(sketch, "E79.18", {"start": v(-60, 40.3) * mm, "end": v(-60, -40.3) * mm});
            skArc(sketch, "E79.19", {"start": v(-60, -40.3) * mm, "mid": v(-58.99, -44.68) * mm, "end": v(-56.15, -48.18) * mm});
            skLineSegment(sketch, "E80", {"start": v(0, 120) * mm, "end": v(0, 90) * mm});
            skLineSegment(sketch, "E81", {"start": v(-15, 120) * mm, "end": v(-15, 108) * mm});
            skLineSegment(sketch, "E82", {"start": v(-15, 108) * mm, "end": v(-33, 90) * mm});
            skLineSegment(sketch, "E83", {"start": v(15, 120) * mm, "end": v(15, 108) * mm});
            skLineSegment(sketch, "E84", {"start": v(15, 108) * mm, "end": v(33, 90) * mm});
            skCircle(sketch, "E85", {"center": v(0, 120) * mm, "radius": 6 * mm});
            skArc(sketch, "E86", {"start": v(15, 120) * mm, "mid": v(0, 135) * mm, "end": v(-15, 120) * mm});
            skLineSegment(sketch, "E87", {"start": v(-80, 0) * mm, "end": v(80, 0) * mm, "construction": true});
            skLineSegment(sketch, "E88.MirrorCS", {"start": v(15, 138) * mm, "end": v(33, 156) * mm});
            skLineSegment(sketch, "E89.MirrorCS", {"start": v(3, 138) * mm, "end": v(15, 138) * mm});
            skLineSegment(sketch, "E90.MirrorCS", {"start": v(3, 108) * mm, "end": v(15, 108) * mm});
            skLineSegment(sketch, "E91.MirrorCS", {"start": v(15, -108) * mm, "end": v(33, -90) * mm});
            skLineSegment(sketch, "E92.MirrorCS", {"start": v(-15, -108) * mm, "end": v(-33, -90) * mm});
            skLineSegment(sketch, "E93.MirrorCS", {"start": v(-15, -120) * mm, "end": v(-15, -108) * mm});
            skLineSegment(sketch, "E94.MirrorCS", {"start": v(15, -120) * mm, "end": v(15, -108) * mm});
            skLineSegment(sketch, "E95.MirrorCS", {"start": v(0, -120) * mm, "end": v(0, -90) * mm});
            skCircle(sketch, "E96.MirrorC", {"center": v(0, -120) * mm, "radius": 6 * mm});
            skArc(sketch, "E97.MirrorCS", {"start": v(15, -120) * mm, "mid": v(0, -135) * mm, "end": v(-15, -120) * mm});
            skSolve(sketch);
        }
        {
            var Q0;
            Q0 = qSketchRegion(id + "F16", true);
            var Q1;
            Q1=makeQuery(id+"F2.opExtrude","CAP_FACE",FACE,{"disambiguationData":[OSD([sQuery(id+"F0.wireOp",EDGE,"E12"),sQuery(id+"F0.wireOp",EDGE,"E13"),sQuery(id+"F0.wireOp",EDGE,"E14"),sQuery(id+"F0.wireOp",EDGE,"E15"),sQuery(id+"F0.wireOp",EDGE,"E17.filletArc"),sQuery(id+"F0.wireOp",EDGE,"E18.filletArc"),sQuery(id+"F0.wireOp",EDGE,"E19.filletArc"),sQuery(id+"F0.wireOp",EDGE,"E20.filletArc"),sQuery(id+"F0.wireOp",EDGE,"E25.0"),sQuery(id+"F0.wireOp",EDGE,"E25.1"),sQuery(id+"F0.wireOp",EDGE,"E25.2"),sQuery(id+"F0.wireOp",EDGE,"E25.3"),sQuery(id+"F0.wireOp",EDGE,"E25.4"),sQuery(id+"F0.wireOp",EDGE,"E25.5"),sQuery(id+"F0.wireOp",EDGE,"E25.6"),sQuery(id+"F0.wireOp",EDGE,"E25.7")])],"isStart":false});
            extrude(context, id + "F17", {"entities" : qUnion([Q0]), "endBound" : BoundingType.UP_TO_SURFACE, "endBoundEntityFace" : qUnion([Q1]), "depth" : 25 * mm});
        }
    });
